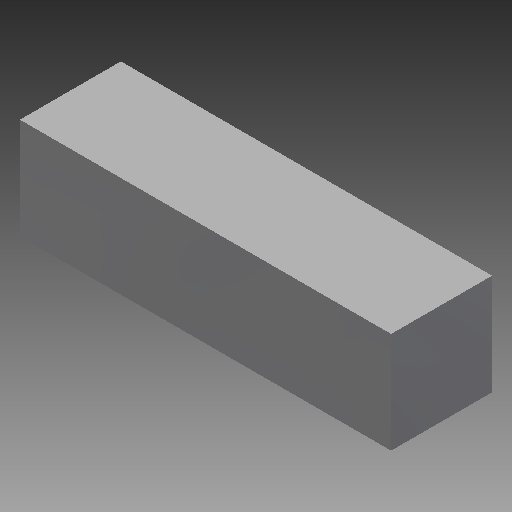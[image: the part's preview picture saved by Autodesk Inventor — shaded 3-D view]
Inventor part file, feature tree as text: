
AUTODESK INVENTOR PART (.ipt)
format: ipt  version: 2017 SP1 (Build 210196100, 196)  size: 118,784 bytes
history: native  units: mm
features: other x5, revolve x1
ambient origin geometry x6: Origin, XZ Plane, XY Plane, X Axis, Y Axis, Z Axis
bodies: Solid1 (feature_tree)
feature tree (6):
  revolve  "Revolution1"  [1 undecoded]
  other  "N-Side1"
  other  "Start Plane"
  other  "Origin point"
  other  "Main Sketch"
  other  "iFeature1:1"
note: 1 required parameter value undecoded (feature->parameter linkage not recoverable at this tier; creation-order binding heuristic only, values carry confidence <= 0.55)
